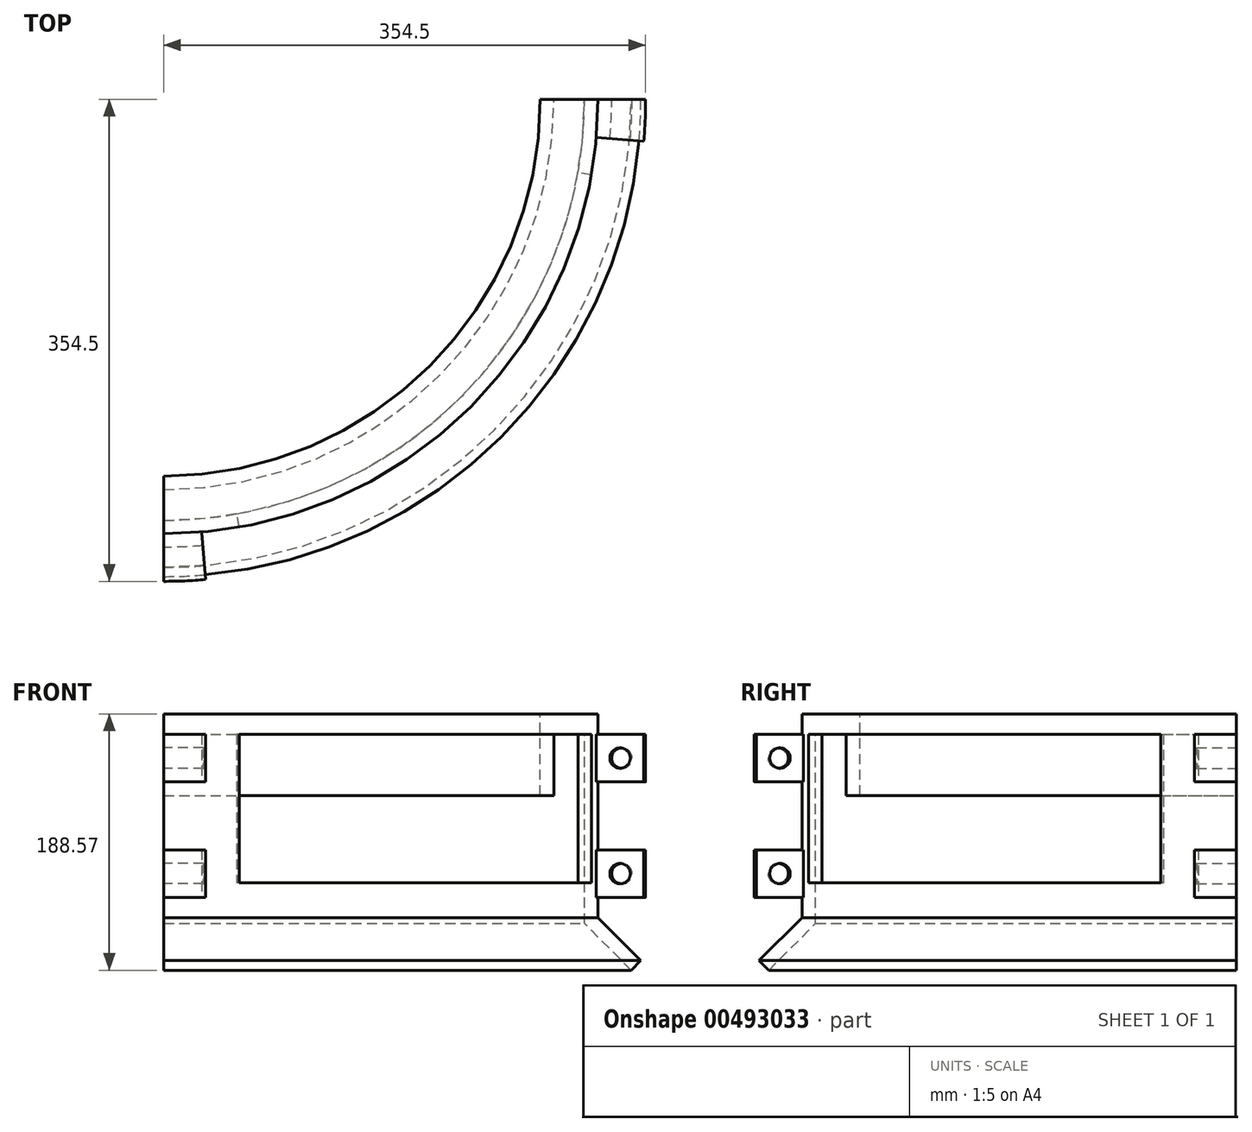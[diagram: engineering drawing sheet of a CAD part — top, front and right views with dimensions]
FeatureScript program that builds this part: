
annotation { "Feature Type Name" : "Feature", "Feature Type Description" : "" }
export const myFeature = defineFeature(function(context is Context, id is Id, definition is map)
    precondition{}
    {
        {
            var Q0;
            Q0=qCreatedBy(makeId("Front.planeOp"),FACE);
            var sketch = newSketch(context, id + "F0", { "sketchPlane" : qUnion([Q0])});
            skLineSegment(sketch, "E0", {"start": v(0, 63.3) * mm, "end": v(0, -86.7) * mm});
            skLineSegment(sketch, "E1", {"start": v(0, -86.7) * mm, "end": v(31.5, -118.2) * mm});
            skLineSegment(sketch, "E2", {"start": v(31.5, -118.2) * mm, "end": v(24.43, -125.27) * mm});
            skLineSegment(sketch, "E3", {"start": v(24.43, -125.27) * mm, "end": v(-10, -90.84) * mm});
            skLineSegment(sketch, "E4", {"start": v(-10, -90.84) * mm, "end": v(-10, 48.3) * mm});
            skLineSegment(sketch, "E5", {"start": v(-10, 48.3) * mm, "end": v(-32.5, 48.3) * mm});
            skLineSegment(sketch, "E6", {"start": v(-32.5, 48.3) * mm, "end": v(-32.5, 3.3) * mm});
            skLineSegment(sketch, "E7", {"start": v(-32.5, 3.3) * mm, "end": v(-42.5, 3.3) * mm});
            skLineSegment(sketch, "E8", {"start": v(-42.5, 3.3) * mm, "end": v(-42.5, 63.3) * mm});
            skLineSegment(sketch, "E9", {"start": v(-42.5, 63.3) * mm, "end": v(0, 63.3) * mm});
            skLineSegment(sketch, "E10", {"start": v(-319.5, 365.07) * mm, "end": v(-319.5, -375.83) * mm});
            skSolve(sketch);
        }
        {
            var Q0;
            Q0=makeQuery(id+"F0.imprint","IMPRINT",FACE,{"disambiguationData":[TD([[makeQuery(id+"F0.imprint","IMPRINT",EDGE,{"derivedFrom":sQuery(id+"F0.wireOp",EDGE,"E0")}),-1.0]])]});
            var Q1;
            Q1=sQuery(id+"F0.wireOp",EDGE,"E10");
            revolve(context, id + "F1", {"entities" : qUnion([Q0]), "axis" : qUnion([Q1]), "revolveType" : RevolveType.ONE_DIRECTION, "angle" : 90 * degree});
        }
        {
            var Q0;
            Q0=makeQuery(id+"F1.opRevolve","CAP_FACE",FACE,{"disambiguationData":[OSD([sQuery(id+"F0.wireOp",EDGE,"E0"),sQuery(id+"F0.wireOp",EDGE,"E1"),sQuery(id+"F0.wireOp",EDGE,"E2"),sQuery(id+"F0.wireOp",EDGE,"E3"),sQuery(id+"F0.wireOp",EDGE,"E4"),sQuery(id+"F0.wireOp",EDGE,"E5"),sQuery(id+"F0.wireOp",EDGE,"E6"),sQuery(id+"F0.wireOp",EDGE,"E7"),sQuery(id+"F0.wireOp",EDGE,"E8"),sQuery(id+"F0.wireOp",EDGE,"E9")])],"isStart":false});
            var sketch = newSketch(context, id + "F2", { "sketchPlane" : qUnion([Q0])});
            skLineSegment(sketch, "E11.bottom", {"start": v(319.5, 48.3) * mm, "end": v(354.5, 48.3) * mm});
            skLineSegment(sketch, "E11.top", {"start": v(319.5, 13.3) * mm, "end": v(354.5, 13.3) * mm});
            skLineSegment(sketch, "E11.left", {"start": v(319.5, 48.3) * mm, "end": v(319.5, 13.3) * mm});
            skLineSegment(sketch, "E11.right", {"start": v(354.5, 48.3) * mm, "end": v(354.5, 13.3) * mm});
            skCircle(sketch, "E12", {"center": v(337, 30.8) * mm, "radius": 7.5 * mm});
            skPoint(sketch, "E12.centerSnap0", {"position": v(337, 48.3) * mm});
            skPoint(sketch, "E12.centerSnap1", {"position": v(319.5, 30.8) * mm});
            skLineSegment(sketch, "E13.bottom", {"start": v(319.5, -36.7) * mm, "end": v(354.5, -36.7) * mm});
            skLineSegment(sketch, "E13.top", {"start": v(319.5, -71.7) * mm, "end": v(354.5, -71.7) * mm});
            skLineSegment(sketch, "E13.left", {"start": v(319.5, -36.7) * mm, "end": v(319.5, -71.7) * mm});
            skLineSegment(sketch, "E13.right", {"start": v(354.5, -36.7) * mm, "end": v(354.5, -71.7) * mm});
            skCircle(sketch, "E14", {"center": v(337, -54.2) * mm, "radius": 7.5 * mm});
            skPoint(sketch, "E14.centerSnap0", {"position": v(337, -36.7) * mm});
            skPoint(sketch, "E14.centerSnap1", {"position": v(319.5, -54.2) * mm});
            skLineSegment(sketch, "E15", {"start": v(0, 230.54) * mm, "end": v(0, -215.96) * mm});
            skSolve(sketch);
        }
        {
            var Q0;
            Q0 = qSketchRegion(id + "F2", true);
            var Q1;
            Q1=sQuery(id+"F2.wireOp",EDGE,"E15");
            revolve(context, id + "F3", {"operationType" : NewBodyOperationType.ADD, "entities" : qUnion([Q0]), "axis" : qUnion([Q1]), "revolveType" : RevolveType.ONE_DIRECTION, "oppositeDirection" : true, "angle" : 5 * degree});
        }
        {
            var Q0;
            Q0 = qSketchRegion(id + "F2", true);
            var Q1;
            Q1=makeQuery(id+"F1.opRevolve","SWEPT_FACE",FACE,{"disambiguationData":[OSD([sQuery(id+"F0.wireOp",EDGE,"E8")])]});
            revolve(context, id + "F4", {"operationType" : NewBodyOperationType.ADD, "entities" : qUnion([Q0]), "axis" : qUnion([Q1]), "revolveType" : RevolveType.TWO_DIRECTIONS, "angle" : 275 * degree, "angleBack" : 270 * degree});
        }
        {
            var Q0;
            Q0=qCreatedBy(makeId("Front.planeOp"),FACE);
            var sketch = newSketch(context, id + "F5", { "sketchPlane" : qUnion([Q0])});
            skLineSegment(sketch, "E16.bottom", {"start": v(0, 48.3) * mm, "end": v(-10, 48.3) * mm});
            skLineSegment(sketch, "E16.top", {"start": v(0, -60.84) * mm, "end": v(-10, -60.84) * mm});
            skLineSegment(sketch, "E16.left", {"start": v(0, 48.3) * mm, "end": v(0, -60.84) * mm});
            skLineSegment(sketch, "E16.right", {"start": v(-10, 48.3) * mm, "end": v(-10, -60.84) * mm});
            skLineSegment(sketch, "E17", {"start": v(-319.5, 127.34) * mm, "end": v(-319.5, -187.15) * mm});
            skSolve(sketch);
        }
        {
            var Q0;
            Q0 = qSketchRegion(id + "F5", true);
            var Q1;
            Q1=sQuery(id+"F5.wireOp",EDGE,"E17");
            revolve(context, id + "F6", {"operationType" : NewBodyOperationType.REMOVE, "entities" : qUnion([Q0]), "axis" : qUnion([Q1]), "revolveType" : RevolveType.TWO_DIRECTIONS, "oppositeDirection" : true, "angle" : 350 * degree, "angleBack" : 280 * degree});
        }
    });
